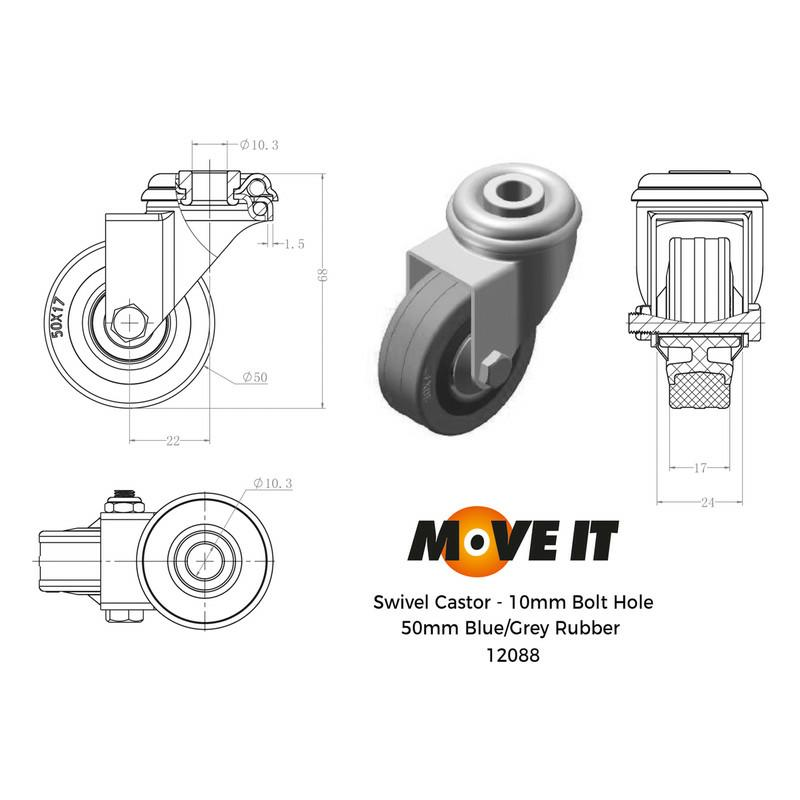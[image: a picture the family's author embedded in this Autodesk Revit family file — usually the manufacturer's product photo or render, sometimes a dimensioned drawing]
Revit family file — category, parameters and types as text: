
# Revit family: ThinkingWall Shelf
name_source: partatom
category: Generic Models
units: mm (PartAtom-declared; Revit-internal decimal feet)

## family parameters
Always vertical = Yes
Can host rebar = No
Cut with Voids When Loaded = No
Maintain Annotation Orientation = No
Part Type = Normal
Room Calculation Point = No
Round Connector Dimension = Use Diameter
Shared = No
Work Plane-Based = No

## types (1)
- ThinkingWall® Shelf
    Acoustic Colour = <By Category>
    Default Elevation = 0 mm  [stored 0 ft]
    Description = Mobile freestanding shelving unit. Part of the ThinkingWall® range for flexible breakout and meeting spaces.
    Length = 1200 mm
    Manufacturer = Logovisual LTD
    Model = ThinkingWall® Shelf
    No of Slat = 31
    Plinth Colour = <By Category>
    Shelf Colour = <By Category>
    Steel Colour = <By Category>
    URL = https://www.logovisual.com

note: [stored X ft] marks values corroborated as IEEE doubles in the binary element streams (Revit-internal decimal feet)

## geometry (parser evidence)
native form markers: Sweep x15
no freeform markers — native parametric forms only
